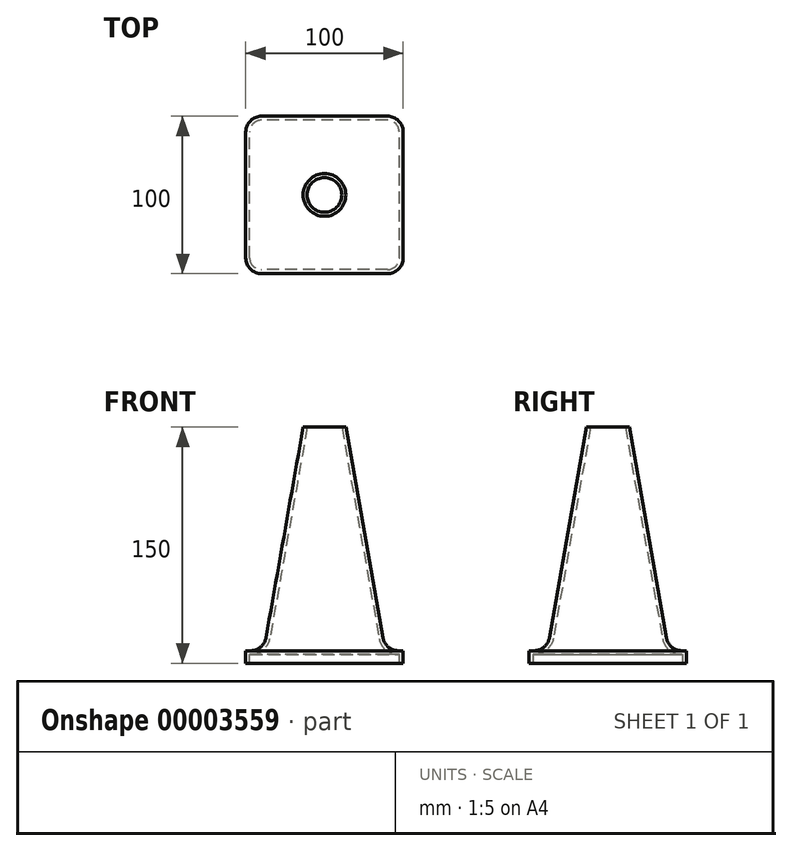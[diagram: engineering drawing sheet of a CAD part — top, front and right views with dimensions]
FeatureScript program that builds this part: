
annotation { "Feature Type Name" : "Feature", "Feature Type Description" : "" }
export const myFeature = defineFeature(function(context is Context, id is Id, definition is map)
    precondition{}
    {
        {
            var Q0;
            Q0=qCreatedBy(makeId("Front.planeOp"),FACE);
            var sketch = newSketch(context, id + "F0", { "sketchPlane" : qUnion([Q0])});
            skLineSegment(sketch, "E0", {"start": v(0, 0) * mm, "end": v(0, 150) * mm});
            skLineSegment(sketch, "E1", {"start": v(0, 150) * mm, "end": v(13.55, 150) * mm});
            skLineSegment(sketch, "E2", {"start": v(13.55, 150) * mm, "end": v(40, 0) * mm});
            skLineSegment(sketch, "E3", {"start": v(40, 0) * mm, "end": v(0, 0) * mm});
            skSolve(sketch);
        }
        {
            var Q0;
            Q0=makeQuery(id+"F0.imprint","IMPRINT",FACE,{"disambiguationData":[TD([[makeQuery(id+"F0.imprint","IMPRINT",EDGE,{"derivedFrom":sQuery(id+"F0.wireOp",EDGE,"E0")}),-1.0]])]});
            var Q1;
            Q1=sQuery(id+"F0.wireOp",EDGE,"E0");
            revolve(context, id + "F1", {"entities" : qUnion([Q0]), "axis" : qUnion([Q1]), "revolveType" : RevolveType.FULL});
        }
        {
            var Q0;
            Q0=makeQuery(id+"F1.opRevolve","SWEPT_FACE",FACE,{"disambiguationData":[OSD([sQuery(id+"F0.wireOp",EDGE,"E3")])]});
            var sketch = newSketch(context, id + "F2", { "sketchPlane" : qUnion([Q0])});
            skLineSegment(sketch, "E4.rect.bottom", {"start": v(50, 50) * mm, "end": v(-50, 50) * mm});
            skLineSegment(sketch, "E4.rect.top", {"start": v(50, -50) * mm, "end": v(-50, -50) * mm});
            skLineSegment(sketch, "E4.rect.left", {"start": v(50, 50) * mm, "end": v(50, -50) * mm});
            skLineSegment(sketch, "E4.rect.right", {"start": v(-50, 50) * mm, "end": v(-50, -50) * mm});
            skPoint(sketch, "E4.rect.middle", {"position": v(0, 0) * mm});
            skSolve(sketch);
        }
        {
            var Q0;
            Q0 = qSketchRegion(id + "F2", true);
            extrude(context, id + "F3", {"entities" : qUnion([Q0]), "operationType" : NewBodyOperationType.ADD, "oppositeDirection" : true, "depth" : 8 * mm});
        }
        {
            var Q0;
            Q0=makeQuery(id+"F3.opExtrude","SWEPT_EDGE",EDGE,{"disambiguationData":[OSD([sQuery(id+"F2.wireOp",EDGE,"E4.rect.bottom"),sQuery(id+"F2.wireOp",EDGE,"E4.rect.left")])]});
            var Q1;
            Q1=makeQuery(id+"F3.opExtrude","SWEPT_EDGE",EDGE,{"disambiguationData":[OSD([sQuery(id+"F2.wireOp",EDGE,"E4.rect.bottom"),sQuery(id+"F2.wireOp",EDGE,"E4.rect.right")])]});
            var Q2;
            Q2=makeQuery(id+"F3.opExtrude","SWEPT_EDGE",EDGE,{"disambiguationData":[OSD([sQuery(id+"F2.wireOp",EDGE,"E4.rect.top"),sQuery(id+"F2.wireOp",EDGE,"E4.rect.right")])]});
            var Q3;
            Q3=makeQuery(id+"F3.opExtrude","SWEPT_EDGE",EDGE,{"disambiguationData":[OSD([sQuery(id+"F2.wireOp",EDGE,"E4.rect.top"),sQuery(id+"F2.wireOp",EDGE,"E4.rect.left")])]});
            fillet(context, id + "F4", {"entities" : qUnion([Q0, Q1, Q2, Q3]), "radius" : 10 * mm, "tangentPropagation" : true, "allowEdgeOverflow" : false});
        }
        {
            var Q0;
            Q0=makeQuery(id+"F3.boolean.opBoolean","INTERSECT",EDGE,{"derivedFrom":[makeQuery(id+"F1.opRevolve","SWEPT_FACE",FACE,{"disambiguationData":[OSD([sQuery(id+"F0.wireOp",EDGE,"E2")])]}),makeQuery(id+"F3.opExtrude","CAP_FACE",FACE,{"disambiguationData":[OSD([sQuery(id+"F2.wireOp",EDGE,"E4.rect.bottom"),sQuery(id+"F2.wireOp",EDGE,"E4.rect.top"),sQuery(id+"F2.wireOp",EDGE,"E4.rect.left"),sQuery(id+"F2.wireOp",EDGE,"E4.rect.right")])],"isStart":false})]});
            fillet(context, id + "F5", {"entities" : qUnion([Q0]), "radius" : 10 * mm, "tangentPropagation" : true, "allowEdgeOverflow" : false});
        }
        {
            var Q0;
            Q0=makeQuery(id+"F3.boolean.opBoolean","MERGE",FACE,{"derivedFrom":[makeQuery(id+"F1.opRevolve","SWEPT_FACE",FACE,{"disambiguationData":[OSD([sQuery(id+"F0.wireOp",EDGE,"E3")])]}),makeQuery(id+"F3.opExtrude","CAP_FACE",FACE,{"disambiguationData":[OSD([sQuery(id+"F2.wireOp",EDGE,"E4.rect.bottom"),sQuery(id+"F2.wireOp",EDGE,"E4.rect.top"),sQuery(id+"F2.wireOp",EDGE,"E4.rect.left"),sQuery(id+"F2.wireOp",EDGE,"E4.rect.right")])],"isStart":true})]});
            var Q1;
            Q1=makeQuery(id+"F1.opRevolve","SWEPT_FACE",FACE,{"disambiguationData":[OSD([sQuery(id+"F0.wireOp",EDGE,"E1")])]});
            shell(context, id + "F6", {"entities" : qUnion([Q0, Q1]), "thickness" : 2.5 * mm});
        }
    });
